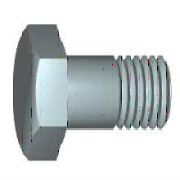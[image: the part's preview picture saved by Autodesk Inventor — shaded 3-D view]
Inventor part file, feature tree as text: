
AUTODESK INVENTOR PART (.ipt)
format: ipt  version: 2023.2 (Build 272271030, 271C)  size: 177,152 bytes
history: native  units: mm
features: sketch x2, revolve x1, thread x1, chamfer x1
ambient origin geometry x8: Origin, YZ Plane, XZ Plane, XY Plane, X Axis, Y Axis, Z Axis, Center Point
bodies: Solid1 (feature_tree)
feature tree (5):
  revolve  "Revolution1"  [1 undecoded]
  thread  "Thread1"  [1 undecoded]
  chamfer  "Chamfer1"  Distance=0.6mm
  sketch  "Sketch1"  dims[d0=19.5mm d1=8.0mm d3=16.0mm]
  sketch  "Sketch2"  dims[d4=11.5mm d5=0.6mm d6=90.0deg d14=15.0mm d15=0.0mm d16=0.666667mm d17=2.0mm d18=45.0deg d19=0.0mm d20=0.0mm d21=0.0mm d22=30.0deg d23=12.35mm d24=5.3mm d25=13.0mm d26=5.3mm d27=0.0mm]
note: 2 required parameter values undecoded (feature->parameter linkage not recoverable at this tier; creation-order binding heuristic only, values carry confidence <= 0.55)